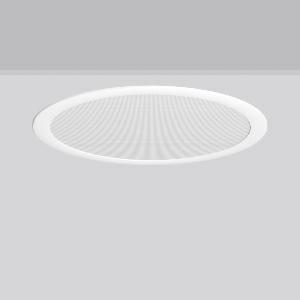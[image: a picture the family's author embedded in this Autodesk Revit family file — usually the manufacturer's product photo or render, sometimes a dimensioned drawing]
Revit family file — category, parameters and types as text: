
# Revit family: toledo_flat_round_e_901586_002_76_fc0c
name_source: partatom
category: Lighting Fixtures
units: mm (PartAtom-declared; Revit-internal decimal feet)

## family parameters
Cut with Voids When Loaded = No
Host = Face
Light Source = No
Part Type = Normal
Room Calculation Point = No
Round Connector Dimension = Use Diameter
Shared = No

## types (1)
- TOLEDO FLAT round E (1 x LED Modul 830, 3450 lm, 3000)
    Apparent Load = 30 VA
    CIE Flux Codes = 62 86 96 100 100
    Color Rendering = 80
    Color Temperature = 3000
    Default Elevation = 1800 mm
    Description = Series: TOLEDO FLAT round
Ultra thin recessed downlight. Housing: die-cast aluminium. Lightguide and diffuser made of non-yellowing PMMA, prismatic. Ceiling installation with spring system. Mounting depth depends on ceiling strength. Including separate LED converter with connecting cable 250 mm. Suitable for through-wiring with separately available accessories. Surface mounted housing as accessory for all sizes. Retrofittable decorative cylinders made of chintz fabric as accessory, optional with satin finish plastic diffuser. Through-wiring box (5 pole) available as accessory. 
Colour: white
Diameter: 495 mm
Height: 6 mm
Cut-out diameter: 470 mm
Recess height: 40-59 mm
Luminaire: recess height: 31-51 mm
Lamp: LED
Socket: without socket
Colour temperature: 3000K
Colour rendering index (CRI): 80
System power: 30 W
Rated luminous flux: 3450 lm
Luminous efficiency: 115 lm/W
Control gear: Converter, dimmable, DALI
Protection class: II
Type of protection: IP 54
    Height = 0 mm  [stored 0 ft]
    Lamp = 1 x LED Modul 830
    Lamp Light Flux = 3450 lm
    Lamp count = 1
    Length = 495 mm
    Lifetime = 50000 h
    Luminous efficacy = 115 lm/W
    Manufacturer = RZB
    ModVariant = No
    Model = 901586.002.76
    Mounting Place = Ceiling
    Mounting Type = Recessed
    Number of Poles = 1
    OnlyDefault = Yes
    Power Factor = 1
    Product Name = TOLEDO FLAT round E
    Product group = Recessed downlights
    ProductGroupID = 402
    Protection Class = Protection class II
    Protection Degree = IP 20
    RLX_Detail_Level = 1
    RLX_Emergency_Light_Flux = 0 lm
    RLX_Emergency_Type = 0
    RLX_Emergency_Type_DB = No
    RlxData = <blob elided: 38285 chars, md5=2e03ec3a>
    Socket = socket
    Standby Power = 0 W
    System Light Flux = 3450 lm
    System Power = 30 W
    Type Comments = Product without accessories
    Type Image = 901586.002.jpg
    URL = http://relux.com
    VarID = ---
    Voltage = 230 V
    Voltage Range = 220-240 V
    Weight = 0.00 kg
    Width = 0 mm  [stored 0 ft]

note: [stored X ft] marks values corroborated as IEEE doubles in the binary element streams (Revit-internal decimal feet)

## geometry (parser evidence)
native form markers: Blend x4, Sweep x10
no freeform markers — native parametric forms only
